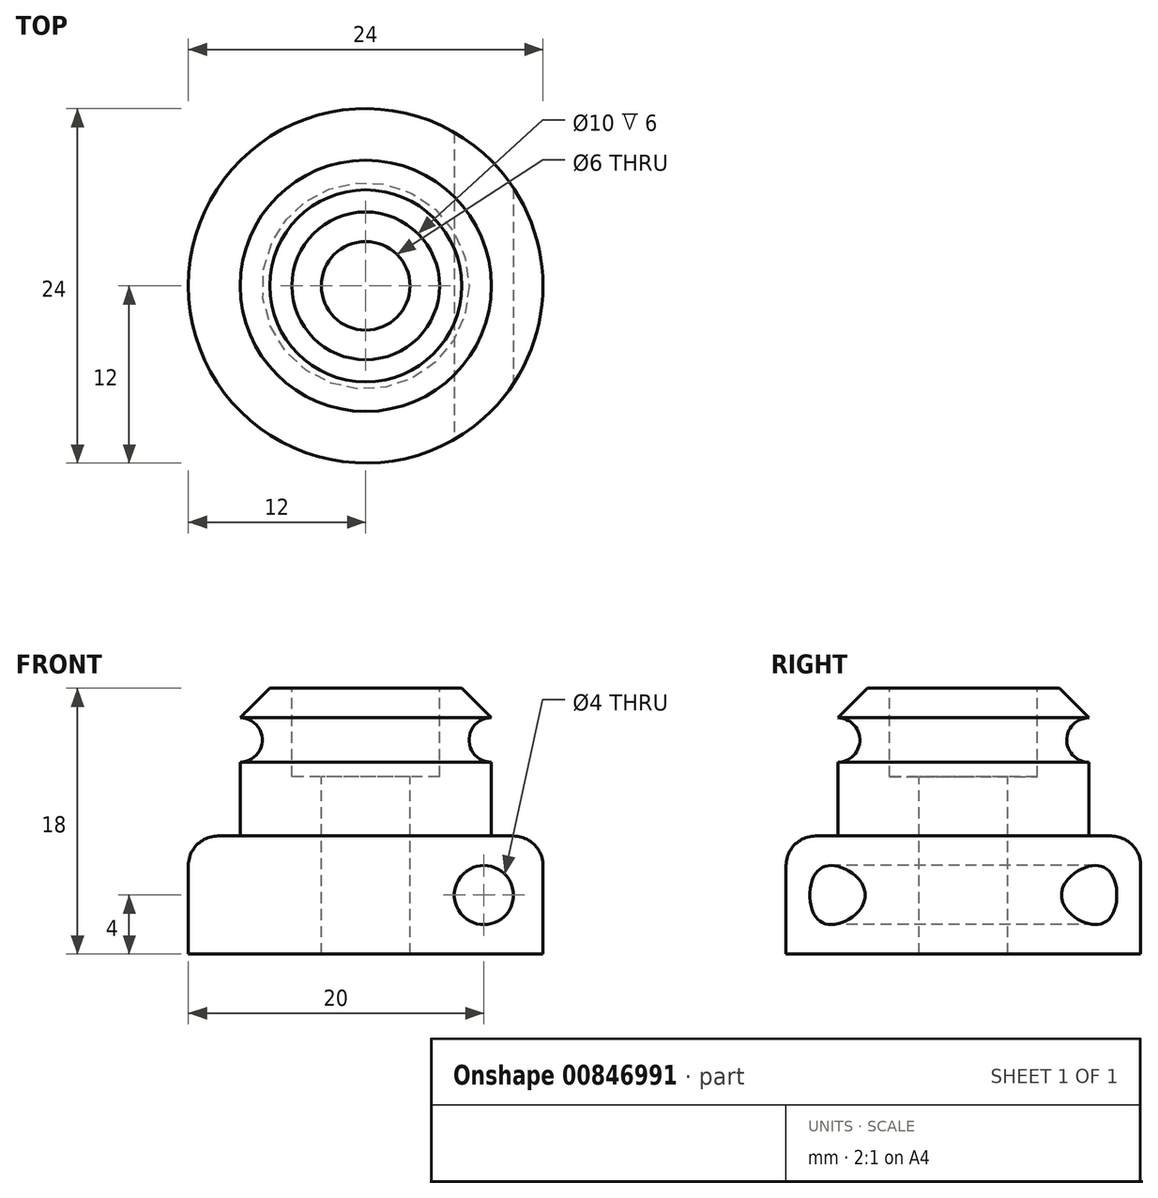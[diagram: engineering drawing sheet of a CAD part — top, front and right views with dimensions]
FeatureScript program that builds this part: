
annotation { "Feature Type Name" : "Feature", "Feature Type Description" : "" }
export const myFeature = defineFeature(function(context is Context, id is Id, definition is map)
    precondition{}
    {
        {
            var Q0;
            Q0=qCreatedBy(makeId("Right.planeOp"),FACE);
            var sketch = newSketch(context, id + "F0", { "sketchPlane" : qUnion([Q0])});
            skLineSegment(sketch, "E0", {"start": v(0, 0) * mm, "end": v(-8.5, 0) * mm});
            skLineSegment(sketch, "E1", {"start": v(-8.5, 0) * mm, "end": v(-8.5, 5) * mm});
            skArc(sketch, "E2", {"start": v(-8.5, 5) * mm, "mid": v(-7, 6.5) * mm, "end": v(-8.5, 8) * mm});
            skLineSegment(sketch, "E3", {"start": v(-8.5, 8) * mm, "end": v(-8.5, 10) * mm});
            skLineSegment(sketch, "E4", {"start": v(-8.5, 10) * mm, "end": v(0, 10) * mm});
            skLineSegment(sketch, "E5", {"start": v(0, 10) * mm, "end": v(0, 0) * mm});
            skSolve(sketch);
        }
        {
            var Q0;
            Q0=makeQuery(id+"F0.imprint","IMPRINT",FACE,{"disambiguationData":[TD([[makeQuery(id+"F0.imprint","IMPRINT",EDGE,{"derivedFrom":sQuery(id+"F0.wireOp",EDGE,"E0")}),-1.0]])]});
            var Q1;
            Q1=sQuery(id+"F0.wireOp",EDGE,"E5");
            revolve(context, id + "F1", {"surfaceOperationType" : NewSurfaceOperationType.NEW, "entities" : qUnion([Q0]), "axis" : qUnion([Q1]), "revolveType" : RevolveType.FULL});
        }
        {
            var Q0;
            Q0=makeQuery(id+"F1.opRevolve","SWEPT_EDGE",EDGE,{"disambiguationData":[OSD([sQuery(id+"F0.wireOp",EDGE,"E3"),sQuery(id+"F0.wireOp",EDGE,"E4")])]});
            chamfer(context, id + "F2", {"entities" : qUnion([Q0]), "width" : 2 * mm, "tangentPropagation" : true});
        }
        {
            var Q0;
            Q0=makeQuery(id+"F1.opRevolve","SWEPT_FACE",FACE,{"disambiguationData":[OSD([sQuery(id+"F0.wireOp",EDGE,"E4")])]});
            var sketch = newSketch(context, id + "F3", { "sketchPlane" : qUnion([Q0])});
            skCircle(sketch, "E6", {"center": v(0, 0) * mm, "radius": 5 * mm});
            skSolve(sketch);
        }
        {
            var Q0;
            Q0 = qSketchRegion(id + "F3", true);
            extrude(context, id + "F4", {"entities" : qUnion([Q0]), "operationType" : NewBodyOperationType.REMOVE, "oppositeDirection" : true, "depth" : 6 * mm, "offsetDistance" : 25 * mm});
        }
        {
            var Q0;
            Q0=makeQuery(id+"F1.opRevolve","SWEPT_FACE",FACE,{"disambiguationData":[OSD([sQuery(id+"F0.wireOp",EDGE,"E0")])]});
            var sketch = newSketch(context, id + "F5", { "sketchPlane" : qUnion([Q0])});
            skCircle(sketch, "E7", {"center": v(0, 0) * mm, "radius": 12 * mm});
            skSolve(sketch);
        }
        {
            var Q0;
            Q0 = qSketchRegion(id + "F5", true);
            extrude(context, id + "F6", {"entities" : qUnion([Q0]), "operationType" : NewBodyOperationType.ADD, "depth" : 8 * mm, "offsetDistance" : 25 * mm});
        }
        {
            var Q0;
            Q0=makeQuery(id+"F4.boolean.opBoolean","COPY",FACE,{"derivedFrom":makeQuery(id+"F4.opExtrude","CAP_FACE",FACE,{"disambiguationData":[OSD([sQuery(id+"F3.wireOp",EDGE,"E6")])],"isStart":false})});
            var sketch = newSketch(context, id + "F7", { "sketchPlane" : qUnion([Q0])});
            skCircle(sketch, "E8", {"center": v(0, 0) * mm, "radius": 3 * mm});
            skSolve(sketch);
        }
        {
            var Q0;
            Q0 = qSketchRegion(id + "F7", true);
            extrude(context, id + "F8", {"entities" : qUnion([Q0]), "operationType" : NewBodyOperationType.REMOVE, "endBound" : BoundingType.UP_TO_NEXT, "oppositeDirection" : true, "depth" : 25 * mm, "offsetDistance" : 25 * mm});
        }
        {
            var Q0;
            Q0=qCreatedBy(makeId("Front.planeOp"),FACE);
            var sketch = newSketch(context, id + "F9", { "sketchPlane" : qUnion([Q0])});
            skCircle(sketch, "E9", {"center": v(8, -4) * mm, "radius": 2 * mm});
            skSolve(sketch);
        }
        {
            var Q0;
            Q0 = qSketchRegion(id + "F9", true);
            extrude(context, id + "F10", {"entities" : qUnion([Q0]), "operationType" : NewBodyOperationType.REMOVE, "endBound" : BoundingType.THROUGH_ALL, "oppositeDirection" : true, "depth" : 25 * mm, "offsetDistance" : 25 * mm, "hasSecondDirection" : true, "secondDirectionBound" : SecondDirectionBoundingType.THROUGH_ALL, "secondDirectionOppositeDirection" : false, "secondDirectionDepth" : 25 * mm});
        }
        {
            var Q0;
            Q0=makeQuery(id+"F6.opExtrude","CAP_EDGE",EDGE,{"disambiguationData":[OSD([sQuery(id+"F5.wireOp",EDGE,"E7")])],"isStart":true});
            fillet(context, id + "F11", {"entities" : qUnion([Q0]), "radius" : 2 * mm, "tangentPropagation" : true, "allowEdgeOverflow" : false});
        }
    });
